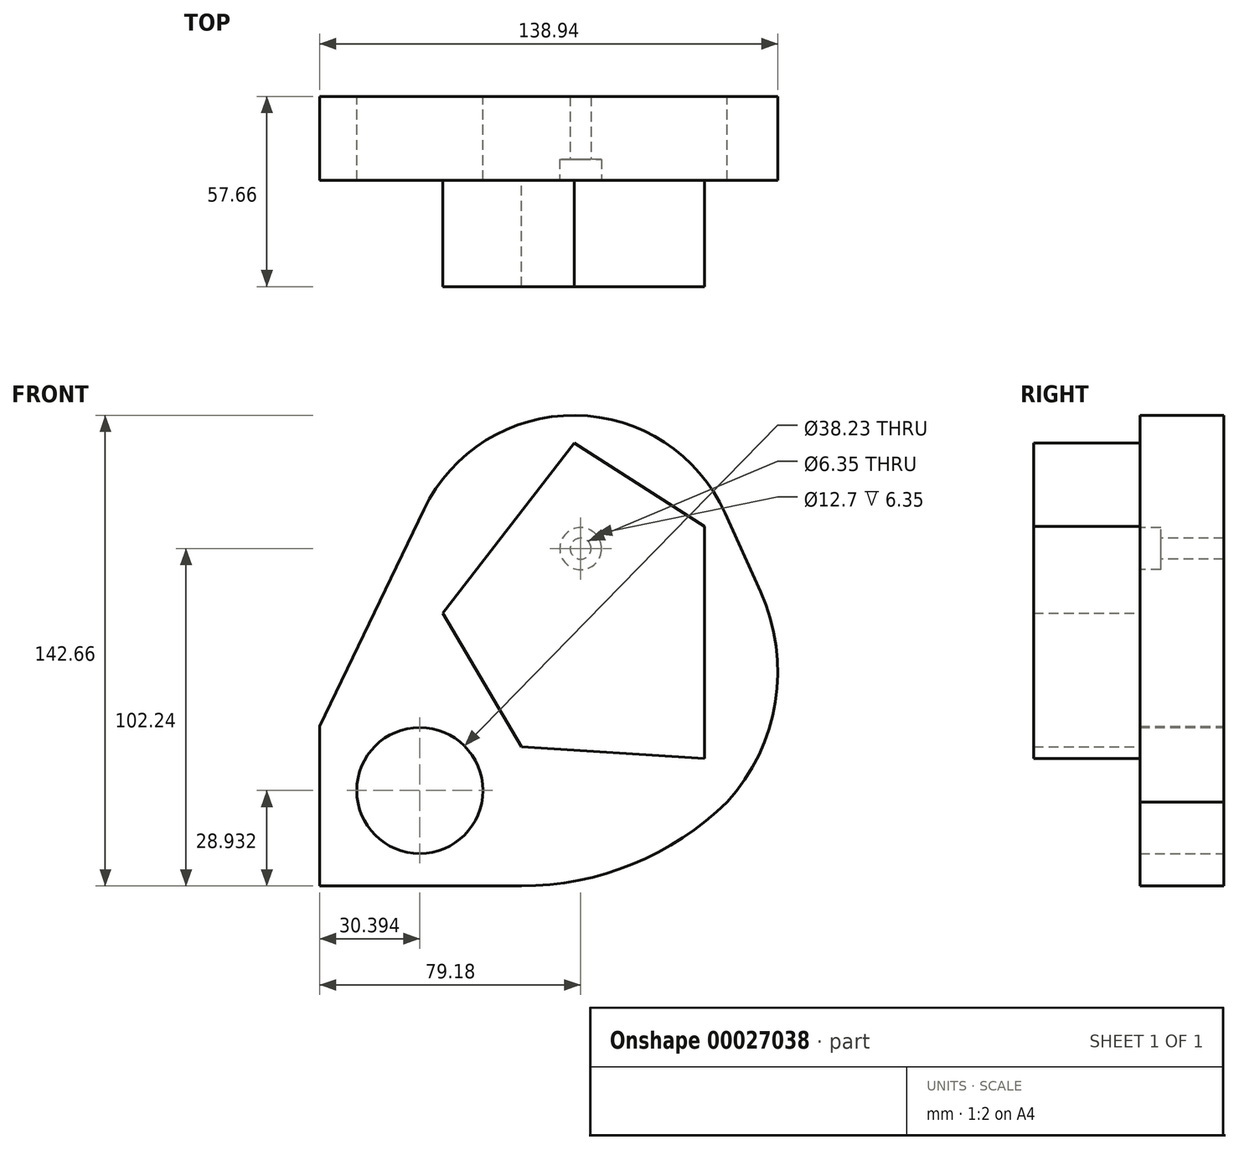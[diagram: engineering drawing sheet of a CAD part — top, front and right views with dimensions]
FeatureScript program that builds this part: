
annotation { "Feature Type Name" : "Feature", "Feature Type Description" : "" }
export const myFeature = defineFeature(function(context is Context, id is Id, definition is map)
    precondition{}
    {
        {
            var Q0;
            Q0=qCreatedBy(makeId("Front.planeOp"),FACE);
            var sketch = newSketch(context, id + "F0", { "sketchPlane" : qUnion([Q0])});
            skLineSegment(sketch, "E0.bottom", {"start": v(0, 0) * mm, "end": v(-61.2, 0) * mm});
            skLineSegment(sketch, "E0.right", {"start": v(-61.2, 0) * mm, "end": v(-61.2, 48.45) * mm});
            skLineSegment(sketch, "E1", {"start": v(-61.2, 48.45) * mm, "end": v(-29.6, 114.1) * mm});
            skArc(sketch, "E2", {"start": v(61.75, 113.03) * mm, "mid": v(16.41, 142.66) * mm, "end": v(-29.6, 114.1) * mm});
            skLineSegment(sketch, "E3", {"start": v(61.75, 113.03) * mm, "end": v(72.53, 89.18) * mm});
            skArc(sketch, "E4", {"start": v(62.4, 25.42) * mm, "mid": v(77.02, 55.78) * mm, "end": v(72.53, 89.18) * mm});
            skArc(sketch, "E5", {"start": v(0, 0) * mm, "mid": v(33.69, 6.6) * mm, "end": v(62.4, 25.42) * mm});
            skCircle(sketch, "E6", {"center": v(-30.8, 28.93) * mm, "radius": 19.12 * mm});
            skSolve(sketch);
        }
        {
            var Q0;
            Q0 = qSketchRegion(id + "F0", true);
            extrude(context, id + "F1", {"entities" : qUnion([Q0]), "depth" : 25.4 * mm});
        }
        {
            var Q0;
            Q0=makeQuery(id+"F1.opExtrude","CAP_FACE",FACE,{"disambiguationData":[OSD([sQuery(id+"F0.wireOp",EDGE,"E0.bottom"),sQuery(id+"F0.wireOp",EDGE,"E0.right"),sQuery(id+"F0.wireOp",EDGE,"E1"),sQuery(id+"F0.wireOp",EDGE,"E2"),sQuery(id+"F0.wireOp",EDGE,"E3"),sQuery(id+"F0.wireOp",EDGE,"E4"),sQuery(id+"F0.wireOp",EDGE,"E5"),sQuery(id+"F0.wireOp",EDGE,"E6")])],"isStart":false});
            var sketch = newSketch(context, id + "F2", { "sketchPlane" : qUnion([Q0])});
            skPoint(sketch, "E7", {"position": v(17.98, 102.24) * mm});
            skPoint(sketch, "E8", {"position": v(-3.94, 88.65) * mm});
            skPoint(sketch, "E9", {"position": v(36.6, 69.39) * mm});
            skSolve(sketch);
        }
        {
            var Q0;
            Q0=sQuery(id+"F2.wireOp",VERTEX,"E7");
            var Q1;
            Q1=makeQuery(id+"F1.opExtrude","SWEPT_BODY",BODY,{"disambiguationData":[OSD([sQuery(id+"F0.wireOp",EDGE,"E0.bottom"),sQuery(id+"F0.wireOp",EDGE,"E0.right"),sQuery(id+"F0.wireOp",EDGE,"E1"),sQuery(id+"F0.wireOp",EDGE,"E2"),sQuery(id+"F0.wireOp",EDGE,"E3"),sQuery(id+"F0.wireOp",EDGE,"E4"),sQuery(id+"F0.wireOp",EDGE,"E5"),sQuery(id+"F0.wireOp",EDGE,"E6")])]});
            hole(context, id + "F3", {"style" : HoleStyle.C_BORE, "endStyle" : HoleEndStyle.THROUGH, "holeDiameter" : 6.35 * mm, "cBoreDiameter" : 12.7 * mm, "cBoreDepth" : 6.35 * mm, "locations" : qUnion([Q0]), "scope" : qUnion([Q1]), "isTappedThrough" : true});
        }
        {
            var Q0;
            Q0=makeQuery(id+"F1.opExtrude","CAP_FACE",FACE,{"disambiguationData":[OSD([sQuery(id+"F0.wireOp",EDGE,"E0.bottom"),sQuery(id+"F0.wireOp",EDGE,"E0.right"),sQuery(id+"F0.wireOp",EDGE,"E1"),sQuery(id+"F0.wireOp",EDGE,"E2"),sQuery(id+"F0.wireOp",EDGE,"E3"),sQuery(id+"F0.wireOp",EDGE,"E4"),sQuery(id+"F0.wireOp",EDGE,"E5"),sQuery(id+"F0.wireOp",EDGE,"E6")])],"isStart":false});
            var sketch = newSketch(context, id + "F4", { "sketchPlane" : qUnion([Q0])});
            skLineSegment(sketch, "E10", {"start": v(-23.88, 82.67) * mm, "end": v(0, 42.15) * mm});
            skLineSegment(sketch, "E11", {"start": v(0, 42.15) * mm, "end": v(55.54, 38.65) * mm});
            skLineSegment(sketch, "E12", {"start": v(55.54, 38.65) * mm, "end": v(55.54, 109.05) * mm});
            skLineSegment(sketch, "E13", {"start": v(55.54, 109.05) * mm, "end": v(16.06, 134.24) * mm});
            skLineSegment(sketch, "E14", {"start": v(16.06, 134.24) * mm, "end": v(-23.88, 82.67) * mm});
            skSolve(sketch);
        }
        {
            var Q0;
            Q0 = qSketchRegion(id + "F4", true);
            extrude(context, id + "F5", {"entities" : qUnion([Q0]), "operationType" : NewBodyOperationType.ADD, "depth" : 32.26 * mm});
        }
    });
